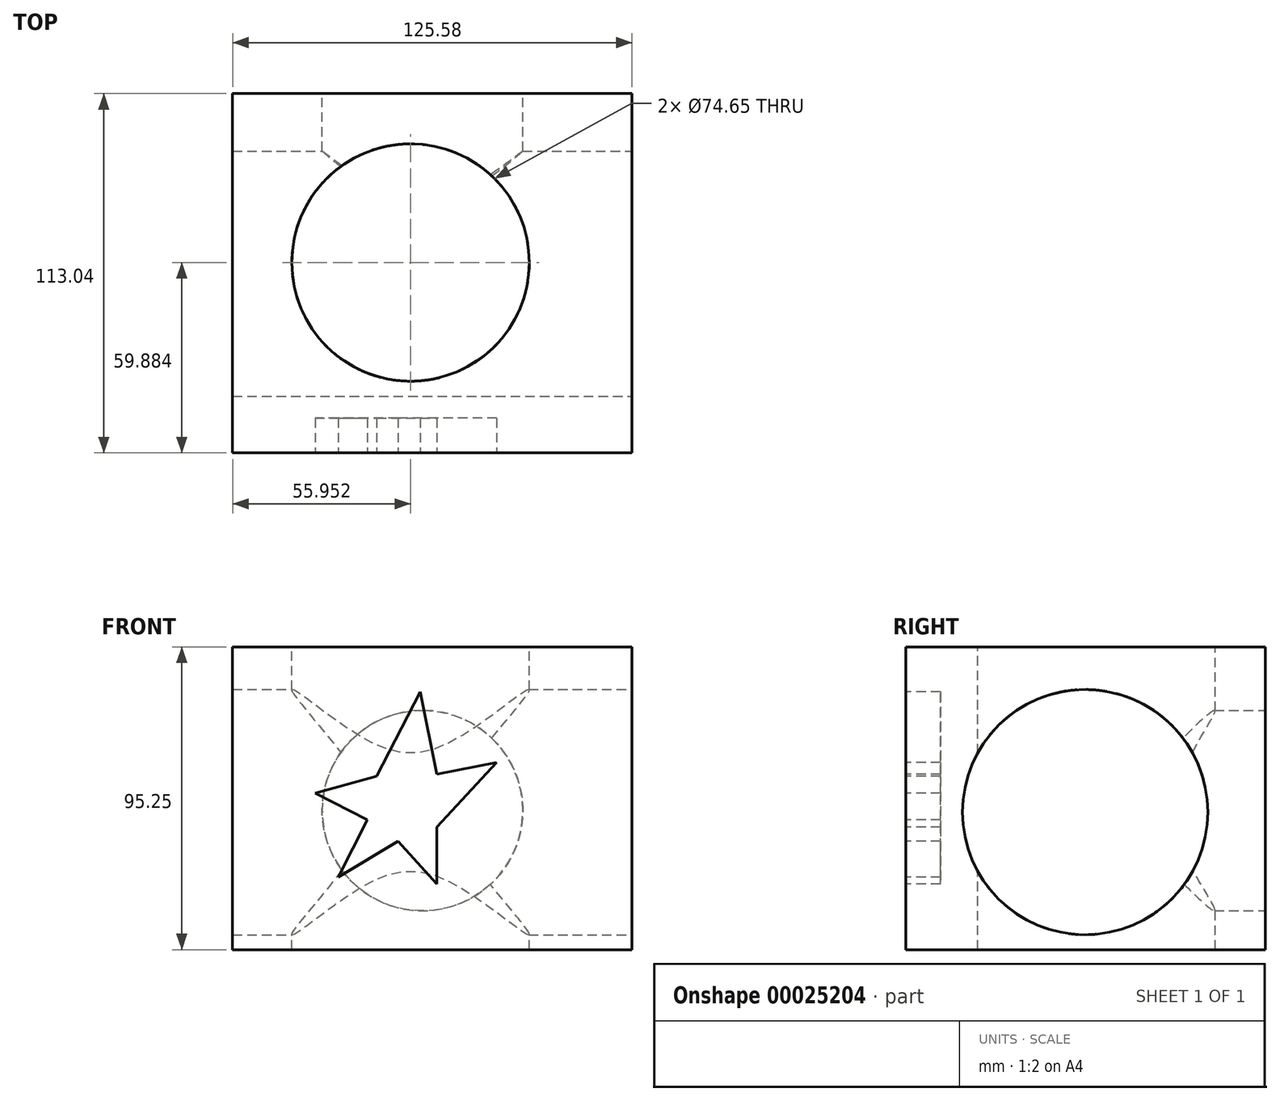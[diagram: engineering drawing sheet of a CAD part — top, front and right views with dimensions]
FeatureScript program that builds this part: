
annotation { "Feature Type Name" : "Feature", "Feature Type Description" : "" }
export const myFeature = defineFeature(function(context is Context, id is Id, definition is map)
    precondition{}
    {
        {
            var Q0;
            Q0=qCreatedBy(makeId("Top.planeOp"),FACE);
            var sketch = newSketch(context, id + "F0", { "sketchPlane" : qUnion([Q0])});
            skLineSegment(sketch, "E0.bottom", {"start": v(-64.23, 53.6) * mm, "end": v(61.35, 53.6) * mm});
            skLineSegment(sketch, "E0.top", {"start": v(-64.23, -59.43) * mm, "end": v(61.35, -59.43) * mm});
            skLineSegment(sketch, "E0.left", {"start": v(-64.23, 53.6) * mm, "end": v(-64.23, -59.43) * mm});
            skLineSegment(sketch, "E0.right", {"start": v(61.35, 53.6) * mm, "end": v(61.35, -59.43) * mm});
            skSolve(sketch);
        }
        {
            var Q0;
            Q0=makeQuery(id+"F0.imprint","IMPRINT",FACE,{"disambiguationData":[TD([[makeQuery(id+"F0.imprint","IMPRINT",EDGE,{"derivedFrom":sQuery(id+"F0.wireOp",EDGE,"E0.bottom")}),-1.0]])]});
            extrude(context, id + "F1", {"entities" : qUnion([Q0]), "depth" : 25.4 * mm});
        }
        {
            var Q0;
            Q0=makeQuery(id+"F1.opExtrude","CAP_FACE",FACE,{"disambiguationData":[OSD([sQuery(id+"F0.wireOp",EDGE,"E0.bottom"),sQuery(id+"F0.wireOp",EDGE,"E0.top"),sQuery(id+"F0.wireOp",EDGE,"E0.left"),sQuery(id+"F0.wireOp",EDGE,"E0.right")])],"isStart":false});
            extrude(context, id + "F2", {"entities" : qUnion([Q0]), "operationType" : NewBodyOperationType.ADD, "depth" : 69.85 * mm});
        }
        {
            var Q0;
            {var subQ0=sQuery(id+"F0.wireOp",EDGE,"E0.top");Q0=makeQuery(id+"F2.boolean.opBoolean","MERGE",FACE,{"derivedFrom":[makeQuery(id+"F1.opExtrude","SWEPT_FACE",FACE,{"disambiguationData":[OSD([subQ0])]}),makeQuery(id+"F2.opExtrude","SWEPT_FACE",FACE,{"disambiguationData":[OSD([subQ0])]})]});}
            var sketch = newSketch(context, id + "F3", { "sketchPlane" : qUnion([Q0])});
            skLineSegment(sketch, "E1", {"start": v(-18.94, 54.62) * mm, "end": v(-5.2, 81.05) * mm});
            skLineSegment(sketch, "E2", {"start": v(-5.2, 81.05) * mm, "end": v(0, 55.15) * mm});
            skLineSegment(sketch, "E3", {"start": v(0, 55.15) * mm, "end": v(18.83, 58.94) * mm});
            skLineSegment(sketch, "E4", {"start": v(18.83, 58.94) * mm, "end": v(0, 38.57) * mm});
            skLineSegment(sketch, "E5", {"start": v(0, 38.57) * mm, "end": v(0, 20.68) * mm});
            skLineSegment(sketch, "E6", {"start": v(0, 20.68) * mm, "end": v(-12.28, 34.07) * mm});
            skLineSegment(sketch, "E7", {"start": v(-12.28, 34.07) * mm, "end": v(-31, 22.85) * mm});
            skLineSegment(sketch, "E8", {"start": v(-31, 22.85) * mm, "end": v(-21.85, 40.88) * mm});
            skLineSegment(sketch, "E9", {"start": v(-21.85, 40.88) * mm, "end": v(-38.3, 49.23) * mm});
            skLineSegment(sketch, "E10", {"start": v(-38.3, 49.23) * mm, "end": v(-18.94, 54.62) * mm});
            skSolve(sketch);
        }
        {
            var Q0;
            Q0=makeQuery(id+"F3.imprint","IMPRINT",FACE,{"disambiguationData":[TD([[makeQuery(id+"F3.imprint","IMPRINT",EDGE,{"derivedFrom":sQuery(id+"F3.wireOp",EDGE,"E1")}),-1.0]])]});
            extrude(context, id + "F4", {"entities" : qUnion([Q0]), "operationType" : NewBodyOperationType.REMOVE, "oppositeDirection" : true, "depth" : 10.9 * mm});
        }
        {
            var Q0;
            Q0=makeQuery(id+"F2.opExtrude","CAP_FACE",FACE,{"disambiguationData":[OSD([sQuery(id+"F0.wireOp",EDGE,"E0.bottom"),sQuery(id+"F0.wireOp",EDGE,"E0.top"),sQuery(id+"F0.wireOp",EDGE,"E0.left"),sQuery(id+"F0.wireOp",EDGE,"E0.right")])],"isStart":false});
            var sketch = newSketch(context, id + "F5", { "sketchPlane" : qUnion([Q0])});
            skCircle(sketch, "E11", {"center": v(-8.28, 0.45) * mm, "radius": 37.33 * mm});
            skPoint(sketch, "E11.first.point", {"position": v(-36.84, 24.49) * mm});
            skPoint(sketch, "E11.second.point", {"position": v(27.97, 9.38) * mm});
            skPoint(sketch, "E11.third.point", {"position": v(3.68, -34.9) * mm});
            skSolve(sketch);
        }
        {
            var Q0;
            Q0=makeQuery(id+"F5.imprint","IMPRINT",FACE,{"disambiguationData":[TD([[makeQuery(id+"F5.imprint","IMPRINT",EDGE,{"derivedFrom":sQuery(id+"F5.wireOp",EDGE,"E11")}),1.0]])]});
            extrude(context, id + "F6", {"entities" : qUnion([Q0]), "operationType" : NewBodyOperationType.REMOVE, "oppositeDirection" : true, "depth" : 169.61 * mm});
        }
        {
            var Q0;
            {var subQ0=sQuery(id+"F0.wireOp",EDGE,"E0.right");Q0=makeQuery(id+"F2.boolean.opBoolean","MERGE",FACE,{"derivedFrom":[makeQuery(id+"F1.opExtrude","SWEPT_FACE",FACE,{"disambiguationData":[OSD([subQ0])]}),makeQuery(id+"F2.opExtrude","SWEPT_FACE",FACE,{"disambiguationData":[OSD([subQ0])]})]});}
            var sketch = newSketch(context, id + "F7", { "sketchPlane" : qUnion([Q0])});
            skCircle(sketch, "E12", {"center": v(-3.05, 43.26) * mm, "radius": 38.55 * mm});
            skSolve(sketch);
        }
        {
            var Q0;
            Q0=makeQuery(id+"F7.imprint","IMPRINT",FACE,{"disambiguationData":[TD([[makeQuery(id+"F7.imprint","IMPRINT",EDGE,{"derivedFrom":sQuery(id+"F7.wireOp",EDGE,"E12")}),1.0]])]});
            extrude(context, id + "F8", {"entities" : qUnion([Q0]), "operationType" : NewBodyOperationType.REMOVE, "oppositeDirection" : true, "depth" : 170 * mm});
        }
        {
            var Q0;
            {var subQ0=sQuery(id+"F0.wireOp",EDGE,"E0.bottom");Q0=makeQuery(id+"F2.boolean.opBoolean","MERGE",FACE,{"derivedFrom":[makeQuery(id+"F1.opExtrude","SWEPT_FACE",FACE,{"disambiguationData":[OSD([subQ0])]}),makeQuery(id+"F2.opExtrude","SWEPT_FACE",FACE,{"disambiguationData":[OSD([subQ0])]})]});}
            var sketch = newSketch(context, id + "F9", { "sketchPlane" : qUnion([Q0])});
            skCircle(sketch, "E13", {"center": v(4.53, 43.74) * mm, "radius": 31.52 * mm});
            skSolve(sketch);
        }
        {
            var Q0;
            Q0=makeQuery(id+"F9.imprint","IMPRINT",FACE,{"disambiguationData":[TD([[makeQuery(id+"F9.imprint","IMPRINT",EDGE,{"derivedFrom":sQuery(id+"F9.wireOp",EDGE,"E13")}),1.0]])]});
            extrude(context, id + "F10", {"entities" : qUnion([Q0]), "operationType" : NewBodyOperationType.REMOVE, "oppositeDirection" : true, "depth" : 74.63 * mm});
        }
    });
